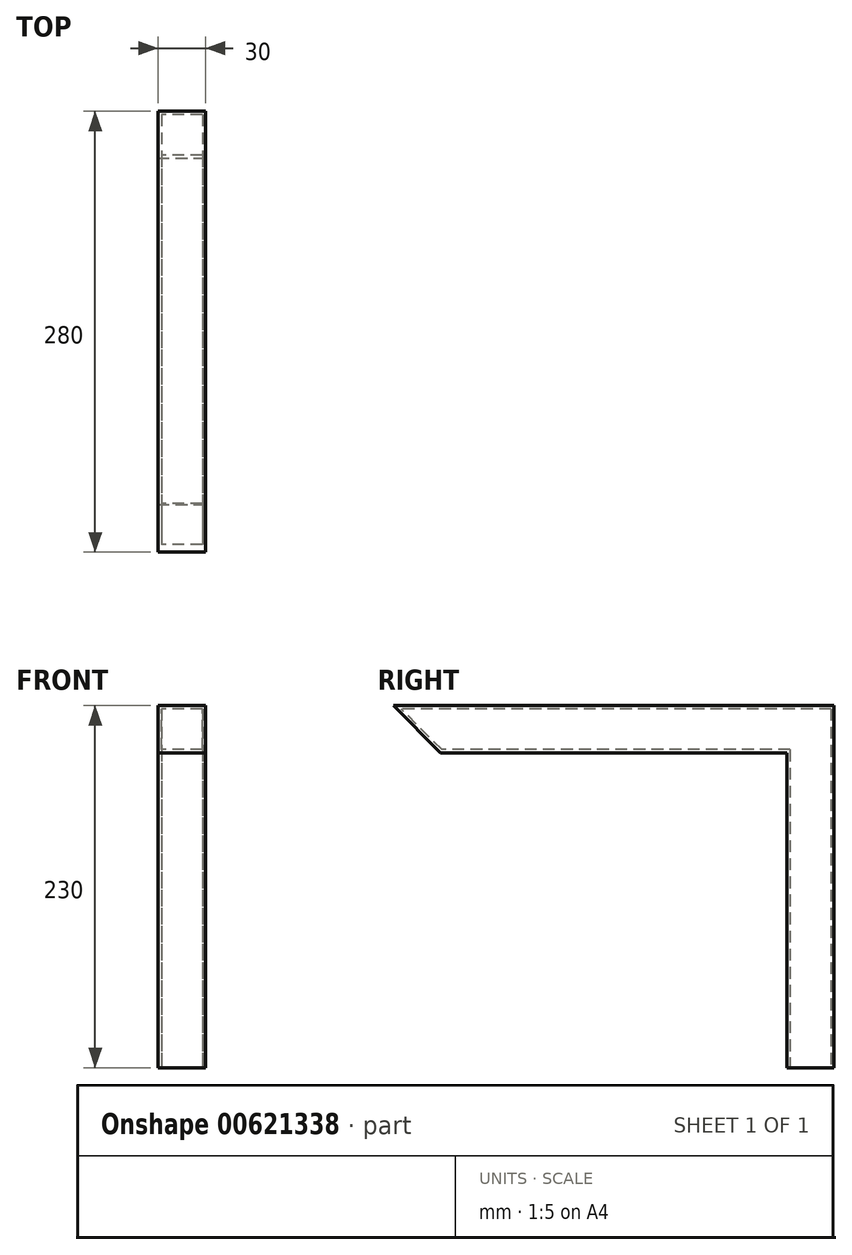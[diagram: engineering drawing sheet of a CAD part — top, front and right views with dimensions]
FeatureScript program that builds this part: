
annotation { "Feature Type Name" : "Feature", "Feature Type Description" : "" }
export const myFeature = defineFeature(function(context is Context, id is Id, definition is map)
    precondition{}
    {
        {
            var Q0;
            Q0=qCreatedBy(makeId("Right.planeOp"),FACE);
            var sketch = newSketch(context, id + "F0", { "sketchPlane" : qUnion([Q0])});
            skLineSegment(sketch, "E0.bottom", {"start": v(140, -15) * mm, "end": v(-140, -15) * mm});
            skLineSegment(sketch, "E0.top", {"start": v(140, 15) * mm, "end": v(-140, 15) * mm});
            skLineSegment(sketch, "E0.left", {"start": v(140, -15) * mm, "end": v(140, 15) * mm});
            skLineSegment(sketch, "E0.right", {"start": v(-140, -15) * mm, "end": v(-140, 15) * mm});
            skPoint(sketch, "E0.middle", {"position": v(0, 0) * mm});
            skLineSegment(sketch, "E1.bottom", {"start": v(140, -15) * mm, "end": v(110, -15) * mm});
            skLineSegment(sketch, "E1.top", {"start": v(140, -215) * mm, "end": v(110, -215) * mm});
            skLineSegment(sketch, "E1.left", {"start": v(140, -15) * mm, "end": v(140, -215) * mm});
            skLineSegment(sketch, "E1.right", {"start": v(110, -15) * mm, "end": v(110, -215) * mm});
            skPoint(sketch, "E2", {"position": v(-110, -15) * mm});
            skLineSegment(sketch, "E3", {"start": v(-110, -15) * mm, "end": v(-140, 15) * mm});
            skSolve(sketch);
        }
        {
            var Q0;
            Q0=makeQuery(id+"F0.imprint","IMPRINT",FACE,{"disambiguationData":[TD([[makeQuery(id+"F0.imprint","IMPRINT",EDGE,{"derivedFrom":sQuery(id+"F0.wireOp",EDGE,"E1.top")}),-1.0]])]});
            var Q1;
            Q1=makeQuery(id+"F0.imprint","IMPRINT",FACE,{"disambiguationData":[TD([[makeQuery(id+"F0.imprint","IMPRINT",EDGE,{"derivedFrom":sQuery(id+"F0.wireOp",EDGE,"E0.top")}),1.0]])]});
            extrude(context, id + "F1", {"entities" : qUnion([Q0, Q1]), "depth" : 30 * mm, "offsetDistance" : 25 * mm});
        }
        {
            var Q0;
            Q0=makeQuery(id+"F1.opExtrude","SWEPT_FACE",FACE,{"disambiguationData":[OSD([sQuery(id+"F0.wireOp",EDGE,"E1.top")])]});
            shell(context, id + "F2", {"entities" : qUnion([Q0]), "thickness" : 2 * mm});
        }
    });
